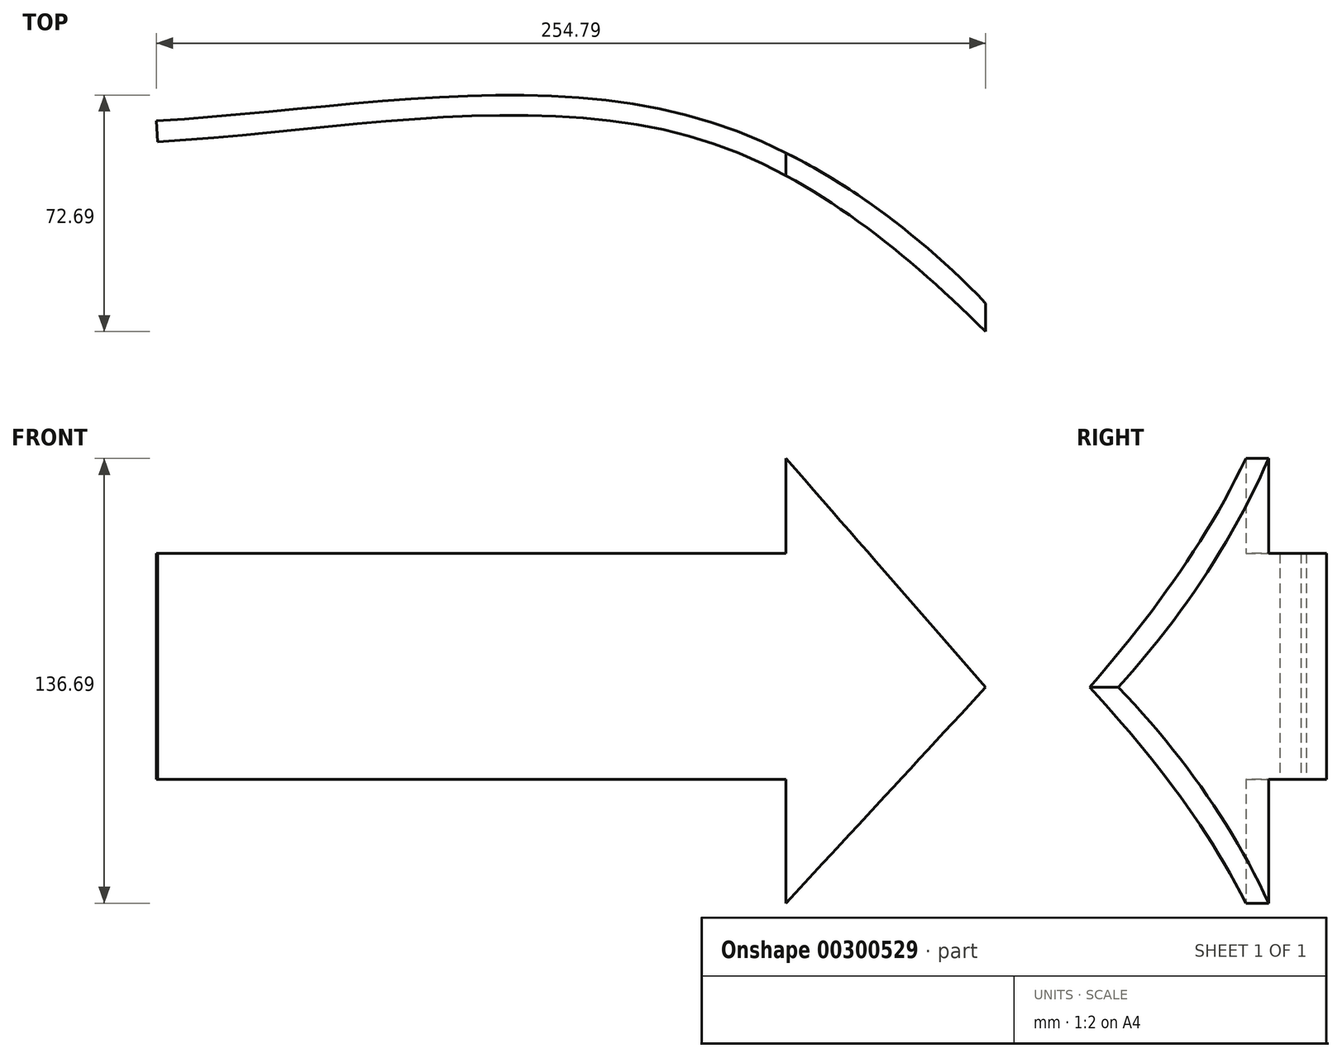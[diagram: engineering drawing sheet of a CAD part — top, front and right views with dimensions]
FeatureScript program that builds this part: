
annotation { "Feature Type Name" : "Feature", "Feature Type Description" : "" }
export const myFeature = defineFeature(function(context is Context, id is Id, definition is map)
    precondition{}
    {
        {
            var Q0;
            Q0=qCreatedBy(makeId("Top.planeOp"),FACE);
            var sketch = newSketch(context, id + "F0", { "sketchPlane" : qUnion([Q0])});
            skFitSpline(sketch, "E0", {"points": [v(-122.57, -6.48) * mm, v(47.78, -6.88) * mm, v(148.9, -82.02) * mm], "startDerivative": vector(317.64, 18.71) * mm, "endDerivative": vector(143.9, -146.78) * mm});
            skFitSpline(sketch, "E1", {"points": [v(-122.88, 0) * mm, v(48.44, -0.72) * mm, v(148.9, -76.34) * mm], "startDerivative": vector(317.48, 18.35) * mm, "endDerivative": vector(112.98, -157.3) * mm});
            skLineSegment(sketch, "E2", {"start": v(148.9, -82.02) * mm, "end": v(148.9, -76.34) * mm});
            skLineSegment(sketch, "E3", {"start": v(-122.57, -6.48) * mm, "end": v(-122.88, 0) * mm});
            skSolve(sketch);
        }
        {
            var Q0;
            Q0 = qSketchRegion(id + "F0", true);
            extrude(context, id + "F1", {"entities" : qUnion([Q0]), "depth" : 152.4 * mm});
        }
        {
            var Q0;
            Q0=qCreatedBy(makeId("Front.planeOp"),FACE);
            var sketch = newSketch(context, id + "F2", { "sketchPlane" : qUnion([Q0])});
            skLineSegment(sketch, "E4.bottom", {"start": v(-132.65, 187.97) * mm, "end": v(70.55, 187.97) * mm});
            skLineSegment(sketch, "E4.top", {"start": v(-132.65, 111.77) * mm, "end": v(70.55, 111.77) * mm});
            skLineSegment(sketch, "E4.left", {"start": v(-132.65, 187.97) * mm, "end": v(-132.65, 111.77) * mm});
            skLineSegment(sketch, "E4.right", {"start": v(70.55, 187.97) * mm, "end": v(70.55, 111.77) * mm});
            skLineSegment(sketch, "E5.bottom", {"start": v(-132.65, 42.37) * mm, "end": v(70.55, 42.37) * mm});
            skLineSegment(sketch, "E5.top", {"start": v(-132.65, -33.83) * mm, "end": v(70.55, -33.83) * mm});
            skLineSegment(sketch, "E5.left", {"start": v(-132.65, 42.37) * mm, "end": v(-132.65, -33.83) * mm});
            skLineSegment(sketch, "E5.right", {"start": v(70.55, 42.37) * mm, "end": v(70.55, -33.83) * mm});
            skLineSegment(sketch, "E6", {"start": v(70.55, 4.27) * mm, "end": v(131.9, 70.64) * mm});
            skLineSegment(sketch, "E7", {"start": v(131.9, 70.64) * mm, "end": v(70.55, 140.96) * mm});
            skLineSegment(sketch, "E8", {"start": v(222.76, 167.83) * mm, "end": v(222.76, -50.38) * mm});
            skLineSegment(sketch, "E9", {"start": v(222.76, -50.38) * mm, "end": v(70.55, -50.38) * mm});
            skLineSegment(sketch, "E10", {"start": v(70.55, -50.38) * mm, "end": v(70.55, 4.27) * mm});
            skLineSegment(sketch, "E11", {"start": v(222.76, 167.83) * mm, "end": v(101.58, 191.28) * mm});
            skLineSegment(sketch, "E12", {"start": v(101.58, 191.28) * mm, "end": v(70.55, 171.98) * mm});
            skLineSegment(sketch, "E13", {"start": v(70.55, 171.98) * mm, "end": v(70.55, 140.96) * mm});
            skSolve(sketch);
        }
        {
            var Q0;
            Q0 = qSketchRegion(id + "F2", true);
            extrude(context, id + "F3", {"entities" : qUnion([Q0]), "operationType" : NewBodyOperationType.REMOVE, "endBound" : BoundingType.THROUGH_ALL, "depth" : 25.4 * mm});
        }
        {
            var Q0;
            Q0 = qSketchRegion(id + "F2", true);
            extrude(context, id + "F4", {"entities" : qUnion([Q0]), "operationType" : NewBodyOperationType.REMOVE, "endBound" : BoundingType.THROUGH_ALL, "oppositeDirection" : true, "depth" : 25.4 * mm});
        }
    });
